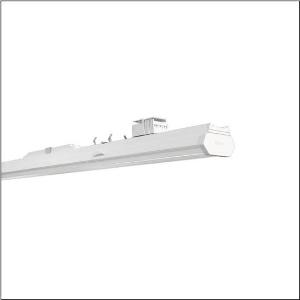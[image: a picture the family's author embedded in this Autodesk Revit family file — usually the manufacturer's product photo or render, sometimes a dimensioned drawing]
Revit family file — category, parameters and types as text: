
# Revit family: licross_11_protected_mo_51td12dn495g
name_source: partatom
category: Lighting Fixtures
units: mm (PartAtom-declared; Revit-internal decimal feet)

## family parameters
Cut with Voids When Loaded = No
Host = Face
Light Source = No
Part Type = Normal
Room Calculation Point = No
Round Connector Dimension = Use Diameter
Shared = No

## types (1)
- --- (1 x LED, 9980 lm, 57.1 W, 4000K)
    Apparent Load = 57 VA
    CIE Flux Codes = 73 92 98 99 100
    Color Rendering = 80
    Color Temperature = 4000K
    Default Elevation = 1800 mm
    Description = Licross 11 Protected MO, luminaire insert, of sheet steel, galvanised, coil coated, white, length: 1.500mm, width: 90mm, height: 101mm, LED rated luminous flux: 9.980lm, light colour: 840, SDCM (Standard Deviation of Colour Matching)MacAdam ≤ 2 SDCM (initial), control gear: DALI 2, with plug, 5-pole, with phase selection, mains connection: 220..240V, AC, 50/60Hz, rated input power: 57W, internal wiring halogen-free, primary optical cover: cover, of PMMA, light emission: direct distribution, primary light characteristic: symmetric, protection rating (complete): IP54, insulation class (complete): insulation class I (protective earthing), certification: CE, ENEC, VDE, UKCA, protection symbol: D if used in an environment with non-conductive dust loads with corresponding accessories, impact resistance: IK06, permissible ambient temperature for indoor applications: -25..+35°C, corresponds to IFS (International Featured Standards) requirements for safety and quality in the food industry, reducing of maximum allowable ambient temperature of 5°C with ceiling mounting, LABS conformity tested according to VDMA 24364:2018-05, The light source and the operating device comply with the requirements of the Ecodesign Regulation (EU) 2019/2020 and are replaceable in accordance with this regulation, packaging unit: 1 piece
    Height = 92 mm
    Lamp = 1 x LED
    Lamp Light Flux = 9980 lm
    Lamp Power = 57.1 W
    Lamp count = 1
    Length = 1500 mm
    Luminous efficacy = 175 lm/W
    Manufacturer = Siteco
    ModVariant = No
    Model = 51TD12DN495G
    Mounting Place = Ceiling
    Mounting Type = Pendant
    Number of Poles = 1
    OnlyDefault = Yes
    Power Factor = 1
    Product Name = Licross 11 Protected MO
    Product group = luminaire insert | ceiling pendant
    ProductGroupID = 901
    Protection Class = Protection class I
    Protection Degree = IP 54
    RLX_Detail_Level = 1
    RLX_Emergency_Light_Flux = 0 lm
    RLX_Emergency_Type = 0
    RLX_Emergency_Type_DB = No
    RlxData = <blob elided: 24749 chars, md5=aad48f22>
    Socket = socket
    Standby Power = 0 W
    System Light Flux = 9980 lm
    System Power = 57 W
    Type Comments = factory setting: luminous flux: 100 % | dim-lin: 254 | 378 mA
    Type Image = l_1256145.jpg
    URL = http://relux.com
    VarID = @adj_104281
    Voltage = 0 V
    Weight = 0.00 kg
    Width = 88 mm

## geometry (parser evidence)
native form markers: Blend x4, Sweep x11
no freeform markers — native parametric forms only
